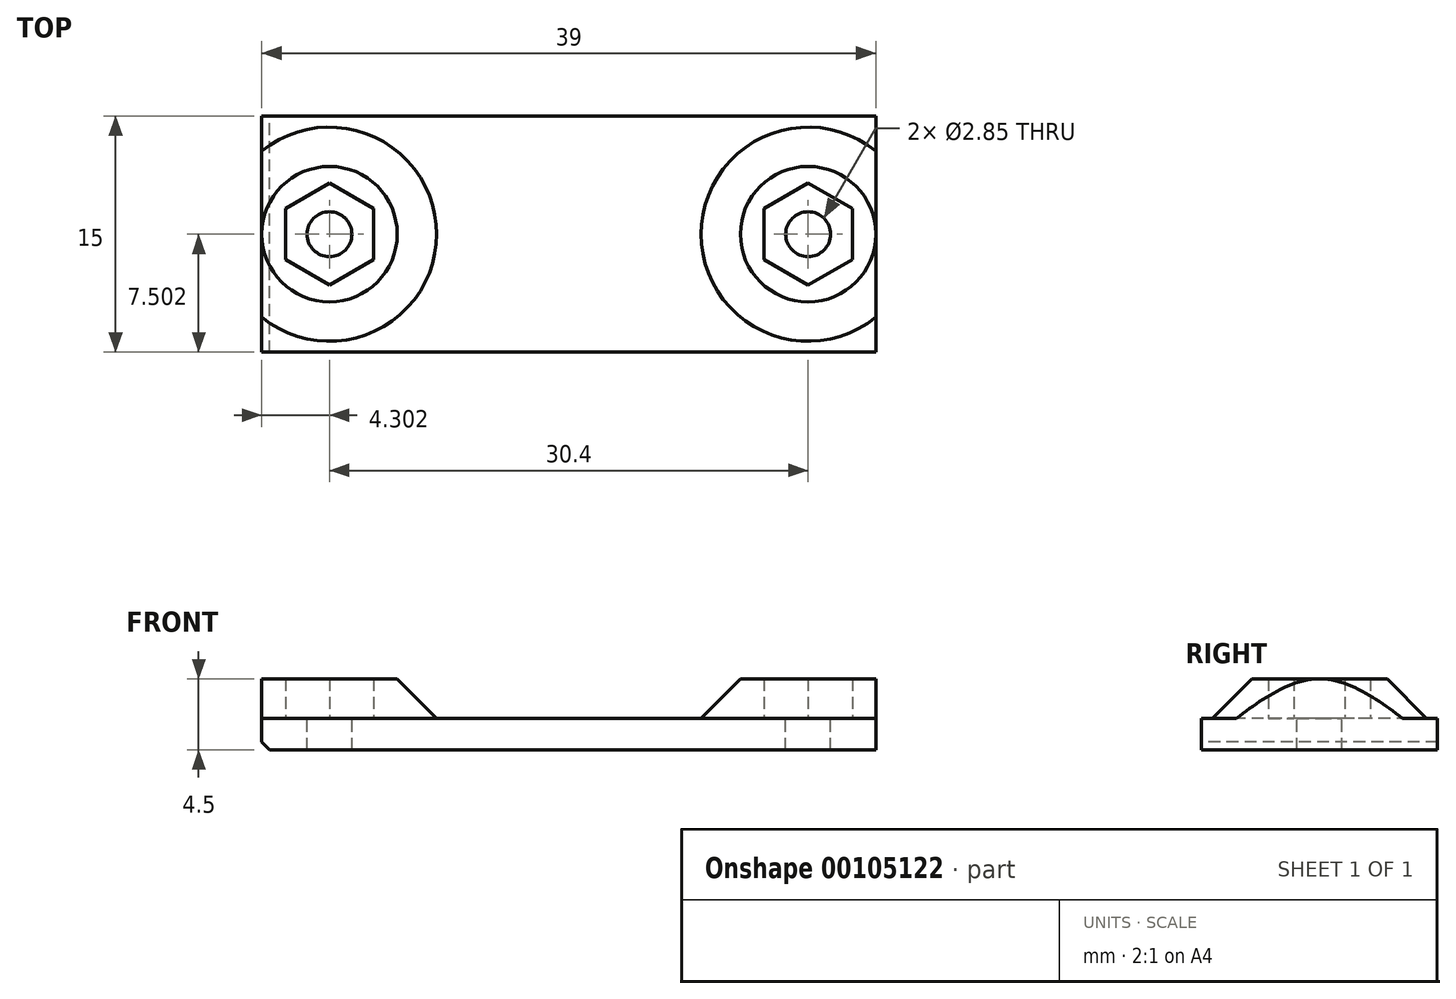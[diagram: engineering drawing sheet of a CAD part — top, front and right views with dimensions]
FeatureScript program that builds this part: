
annotation { "Feature Type Name" : "Feature", "Feature Type Description" : "" }
export const myFeature = defineFeature(function(context is Context, id is Id, definition is map)
    precondition{}
    {
        {
            var Q0;
            Q0=qCreatedBy(makeId("Top.planeOp"),FACE);
            var sketch = newSketch(context, id + "F0", { "sketchPlane" : qUnion([Q0])});
            skLineSegment(sketch, "E0.bottom", {"start": v(-63.62, -8.87) * mm, "end": v(-24.62, -8.87) * mm});
            skLineSegment(sketch, "E0.top", {"start": v(-63.62, -23.87) * mm, "end": v(-24.62, -23.87) * mm});
            skLineSegment(sketch, "E0.left", {"start": v(-63.62, -8.87) * mm, "end": v(-63.62, -23.87) * mm});
            skLineSegment(sketch, "E0.right", {"start": v(-24.62, -8.87) * mm, "end": v(-24.62, -23.87) * mm});
            skLineSegment(sketch, "E1", {"start": v(-63.62, -16.37) * mm, "end": v(-24.62, -16.37) * mm, "construction": true});
            skPoint(sketch, "E2", {"position": v(-44.12, -16.37) * mm});
            skPoint(sketch, "E3", {"position": v(-59.32, -16.37) * mm});
            skPoint(sketch, "E4", {"position": v(-28.92, -16.37) * mm});
            skCircle(sketch, "E5.cCircle", {"center": v(-59.32, -16.37) * mm, "radius": 2.8 * mm, "construction": true});
            skLineSegment(sketch, "E5.0", {"start": v(-56.52, -14.75) * mm, "end": v(-56.52, -17.98) * mm});
            skLineSegment(sketch, "E5.1", {"start": v(-56.52, -17.98) * mm, "end": v(-59.32, -19.6) * mm});
            skLineSegment(sketch, "E5.2", {"start": v(-59.32, -19.6) * mm, "end": v(-62.12, -17.98) * mm});
            skLineSegment(sketch, "E5.3", {"start": v(-62.12, -17.98) * mm, "end": v(-62.12, -14.75) * mm});
            skLineSegment(sketch, "E5.4", {"start": v(-62.12, -14.75) * mm, "end": v(-59.32, -13.14) * mm});
            skLineSegment(sketch, "E5.5", {"start": v(-59.32, -13.14) * mm, "end": v(-56.52, -14.75) * mm});
            skPoint(sketch, "E5.0.midPoint", {"position": v(-56.52, -16.37) * mm});
            skCircle(sketch, "E6.cCircle", {"center": v(-28.92, -16.37) * mm, "radius": 2.8 * mm, "construction": true});
            skLineSegment(sketch, "E6.0", {"start": v(-26.12, -14.75) * mm, "end": v(-26.12, -17.98) * mm});
            skLineSegment(sketch, "E6.1", {"start": v(-26.12, -17.98) * mm, "end": v(-28.92, -19.6) * mm});
            skLineSegment(sketch, "E6.2", {"start": v(-28.92, -19.6) * mm, "end": v(-31.72, -17.98) * mm});
            skLineSegment(sketch, "E6.3", {"start": v(-31.72, -17.98) * mm, "end": v(-31.72, -14.75) * mm});
            skLineSegment(sketch, "E6.4", {"start": v(-31.72, -14.75) * mm, "end": v(-28.92, -13.14) * mm});
            skLineSegment(sketch, "E6.5", {"start": v(-28.92, -13.14) * mm, "end": v(-26.12, -14.75) * mm});
            skPoint(sketch, "E6.0.midPoint", {"position": v(-26.12, -16.37) * mm});
            skCircle(sketch, "E7", {"center": v(-59.32, -16.37) * mm, "radius": 4.3 * mm});
            skCircle(sketch, "E8", {"center": v(-28.92, -16.37) * mm, "radius": 4.3 * mm});
            skSolve(sketch);
        }
        {
            var Q0;
            Q0 = qSketchRegion(id + "F0", true);
            var Q1;
            Q1=makeQuery(id+"F0.imprint","IMPRINT",FACE,{"disambiguationData":[TD([[makeQuery(id+"F0.imprint","IMPRINT",EDGE,{"derivedFrom":sQuery(id+"F0.wireOp",EDGE,"E5.0")}),-1.0]])]});
            var Q2;
            Q2=makeQuery(id+"F0.imprint","IMPRINT",FACE,{"disambiguationData":[TD([[makeQuery(id+"F0.imprint","IMPRINT",EDGE,{"derivedFrom":sQuery(id+"F0.wireOp",EDGE,"E6.0")}),-1.0]])]});
            extrude(context, id + "F1", {"entities" : qUnion([Q0, Q1, Q2]), "oppositeDirection" : true, "depth" : 2 * mm});
        }
        {
            var Q0;
            Q0=sQuery(id+"F0.wireOp",VERTEX,"E3");
            var Q1;
            Q1=sQuery(id+"F0.wireOp",VERTEX,"E4");
            var Q2;
            Q2=makeQuery(id+"F1.opExtrude","SWEPT_BODY",BODY,{"disambiguationData":[OSD([sQuery(id+"F0.wireOp",EDGE,"E0.bottom"),sQuery(id+"F0.wireOp",EDGE,"E0.top"),sQuery(id+"F0.wireOp",EDGE,"E0.left"),sQuery(id+"F0.wireOp",EDGE,"E0.right")])]});
            hole(context, id + "F2", {"style" : HoleStyle.SIMPLE, "endStyle" : HoleEndStyle.BLIND, "holeDiameter" : 2.85 * mm, "holeDepth" : 11 * mm, "locations" : qUnion([Q0, Q1]), "scope" : qUnion([Q2])});
        }
        {
            var Q0;
            Q0=makeQuery(id+"F0.imprint","IMPRINT",FACE,{"disambiguationData":[TD([[makeQuery(id+"F0.imprint","IMPRINT",EDGE,{"derivedFrom":sQuery(id+"F0.wireOp",EDGE,"E5.0")}),1.0]])]});
            var Q1;
            Q1=makeQuery(id+"F0.imprint","IMPRINT",FACE,{"disambiguationData":[TD([[makeQuery(id+"F0.imprint","IMPRINT",EDGE,{"derivedFrom":sQuery(id+"F0.wireOp",EDGE,"E6.0")}),1.0]])]});
            extrude(context, id + "F3", {"entities" : qUnion([Q0, Q1]), "operationType" : NewBodyOperationType.ADD, "depth" : 2.5 * mm});
        }
        {
            var Q0;
            Q0=makeQuery(id+"F3.opExtrude","CAP_EDGE",EDGE,{"disambiguationData":[OSD([sQuery(id+"F0.wireOp",EDGE,"E7")])],"isStart":true});
            var Q1;
            Q1=makeQuery(id+"F3.opExtrude","CAP_EDGE",EDGE,{"disambiguationData":[OSD([sQuery(id+"F0.wireOp",EDGE,"E8")])],"isStart":true});
            chamfer(context, id + "F4", {"entities" : qUnion([Q0, Q1]), "width" : 2.5 * mm, "tangentPropagation" : true});
        }
        {
            var Q0;
            Q0=makeQuery(id+"F1.opExtrude","CAP_EDGE",EDGE,{"disambiguationData":[OSD([sQuery(id+"F0.wireOp",EDGE,"E0.left")])],"isStart":false});
            chamfer(context, id + "F5", {"entities" : qUnion([Q0]), "width" : 0.5 * mm, "tangentPropagation" : true});
        }
    });
